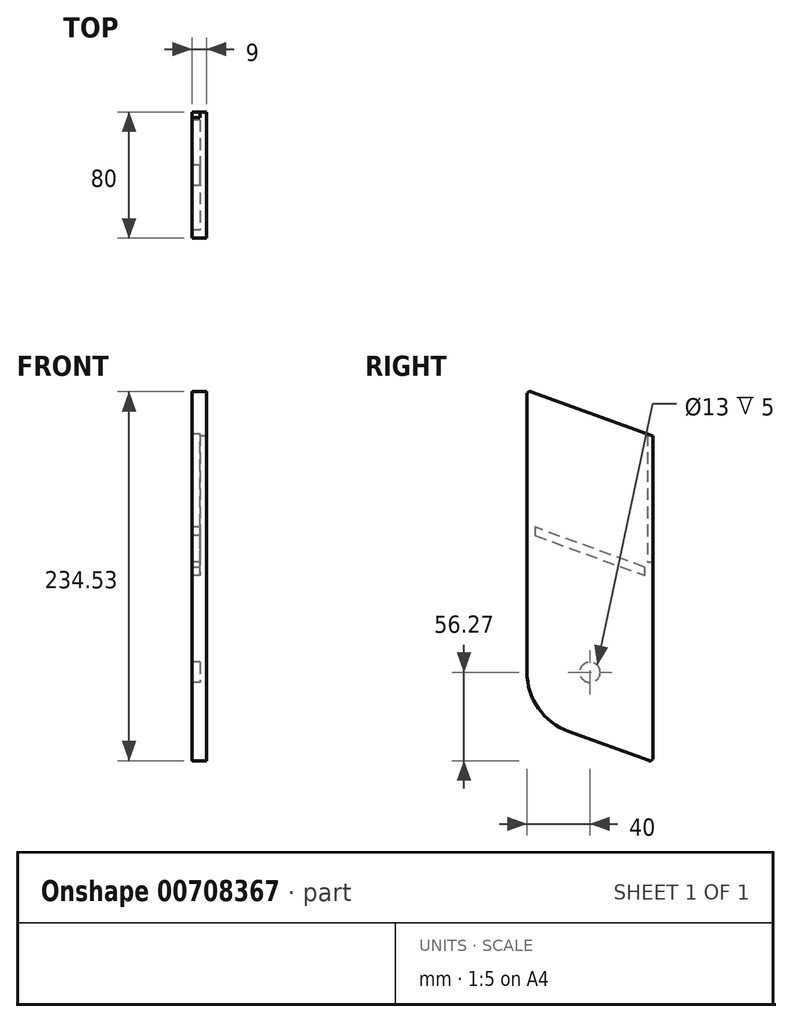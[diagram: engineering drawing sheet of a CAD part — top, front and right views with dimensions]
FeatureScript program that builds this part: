
annotation { "Feature Type Name" : "Feature", "Feature Type Description" : "" }
export const myFeature = defineFeature(function(context is Context, id is Id, definition is map)
    precondition{}
    {
        {
            var Q0;
            Q0=qCreatedBy(makeId("Right.planeOp"),FACE);
            var sketch = newSketch(context, id + "F0", { "sketchPlane" : qUnion([Q0])});
            skLineSegment(sketch, "E0", {"start": v(0, 0) * mm, "end": v(-80, 29.12) * mm});
            skLineSegment(sketch, "E1", {"start": v(-80, 29.12) * mm, "end": v(-80, -150) * mm});
            skLineSegment(sketch, "E2", {"start": v(-53.68, -187.59) * mm, "end": v(0, -207.13) * mm});
            skLineSegment(sketch, "E3", {"start": v(0, -207.13) * mm, "end": v(0, 0) * mm});
            skPoint(sketch, "E4.visualSharp", {"position": v(-80, -178) * mm});
            skArc(sketch, "E4.filletArc", {"start": v(-80, -150) * mm, "mid": v(-72.77, -172.94) * mm, "end": v(-53.68, -187.59) * mm});
            skSolve(sketch);
        }
        {
            var Q0;
            Q0 = qSketchRegion(id + "F0", true);
            extrude(context, id + "F1", {"entities" : qUnion([Q0]), "depth" : 9 * mm, "offsetDistance" : 25 * mm});
        }
        {
            var Q0;
            Q0=makeQuery(id+"F1.opExtrude","CAP_FACE",FACE,{"disambiguationData":[OSD([sQuery(id+"F0.wireOp",EDGE,"E0"),sQuery(id+"F0.wireOp",EDGE,"E1"),sQuery(id+"F0.wireOp",EDGE,"E2"),sQuery(id+"F0.wireOp",EDGE,"E3"),sQuery(id+"F0.wireOp",EDGE,"E4.filletArc")])],"isStart":true});
            var sketch = newSketch(context, id + "F2", { "sketchPlane" : qUnion([Q0])});
            skCircle(sketch, "E5", {"center": v(40, -150) * mm, "radius": 6.5 * mm});
            skSolve(sketch);
        }
        {
            var Q0;
            Q0 = qSketchRegion(id + "F2", true);
            extrude(context, id + "F3", {"entities" : qUnion([Q0]), "operationType" : NewBodyOperationType.REMOVE, "oppositeDirection" : true, "depth" : 5 * mm, "offsetDistance" : 25 * mm});
        }
        {
            var Q0;
            Q0=makeQuery(id+"F1.opExtrude","CAP_FACE",FACE,{"disambiguationData":[OSD([sQuery(id+"F0.wireOp",EDGE,"E0"),sQuery(id+"F0.wireOp",EDGE,"E1"),sQuery(id+"F0.wireOp",EDGE,"E2"),sQuery(id+"F0.wireOp",EDGE,"E3"),sQuery(id+"F0.wireOp",EDGE,"E4.filletArc")])],"isStart":true});
            var sketch = newSketch(context, id + "F4", { "sketchPlane" : qUnion([Q0])});
            skLineSegment(sketch, "E6", {"start": v(5, -83.31) * mm, "end": v(75, -57.84) * mm});
            skLineSegment(sketch, "E7", {"start": v(75, -57.84) * mm, "end": v(75, -63.16) * mm});
            skLineSegment(sketch, "E8", {"start": v(75, -63.16) * mm, "end": v(5, -88.64) * mm});
            skLineSegment(sketch, "E9", {"start": v(5, -88.64) * mm, "end": v(5, -83.31) * mm});
            skSolve(sketch);
        }
        {
            var Q0;
            Q0 = qSketchRegion(id + "F4", true);
            extrude(context, id + "F5", {"entities" : qUnion([Q0]), "operationType" : NewBodyOperationType.REMOVE, "oppositeDirection" : true, "depth" : 5 * mm, "offsetDistance" : 25 * mm});
        }
        {
            var Q0;
            Q0=makeQuery(id+"F1.opExtrude","SWEPT_EDGE",EDGE,{"disambiguationData":[OSD([sQuery(id+"F0.wireOp",EDGE,"E2"),sQuery(id+"F0.wireOp",EDGE,"E3")])]});
            var Q1;
            Q1=makeQuery(id+"F1.opExtrude","SWEPT_EDGE",EDGE,{"disambiguationData":[OSD([sQuery(id+"F0.wireOp",EDGE,"E0"),sQuery(id+"F0.wireOp",EDGE,"E1")])]});
            fillet(context, id + "F6", {"entities" : qUnion([Q0, Q1]), "radius" : 2 * mm, "tangentPropagation" : true, "allowEdgeOverflow" : false});
        }
        {
            var Q0;
            Q0=makeQuery(id+"F1.opExtrude","CAP_FACE",FACE,{"disambiguationData":[OSD([sQuery(id+"F0.wireOp",EDGE,"E0"),sQuery(id+"F0.wireOp",EDGE,"E1"),sQuery(id+"F0.wireOp",EDGE,"E2"),sQuery(id+"F0.wireOp",EDGE,"E3"),sQuery(id+"F0.wireOp",EDGE,"E4.filletArc")])],"isStart":true});
            var sketch = newSketch(context, id + "F7", { "sketchPlane" : qUnion([Q0])});
            skLineSegment(sketch, "E10", {"start": v(3.5, 1.27) * mm, "end": v(3.5, -80) * mm});
            skLineSegment(sketch, "E11", {"start": v(3.5, -80) * mm, "end": v(0, -80) * mm});
            skLineSegment(sketch, "E12", {"start": v(0, -80) * mm, "end": v(0, 0) * mm});
            skLineSegment(sketch, "E13", {"start": v(0, 0) * mm, "end": v(3.5, 1.27) * mm});
            skSolve(sketch);
        }
        {
            var Q0;
            Q0 = qSketchRegion(id + "F7", true);
            extrude(context, id + "F8", {"entities" : qUnion([Q0]), "operationType" : NewBodyOperationType.REMOVE, "oppositeDirection" : true, "depth" : 5 * mm, "offsetDistance" : 25 * mm});
        }
    });
